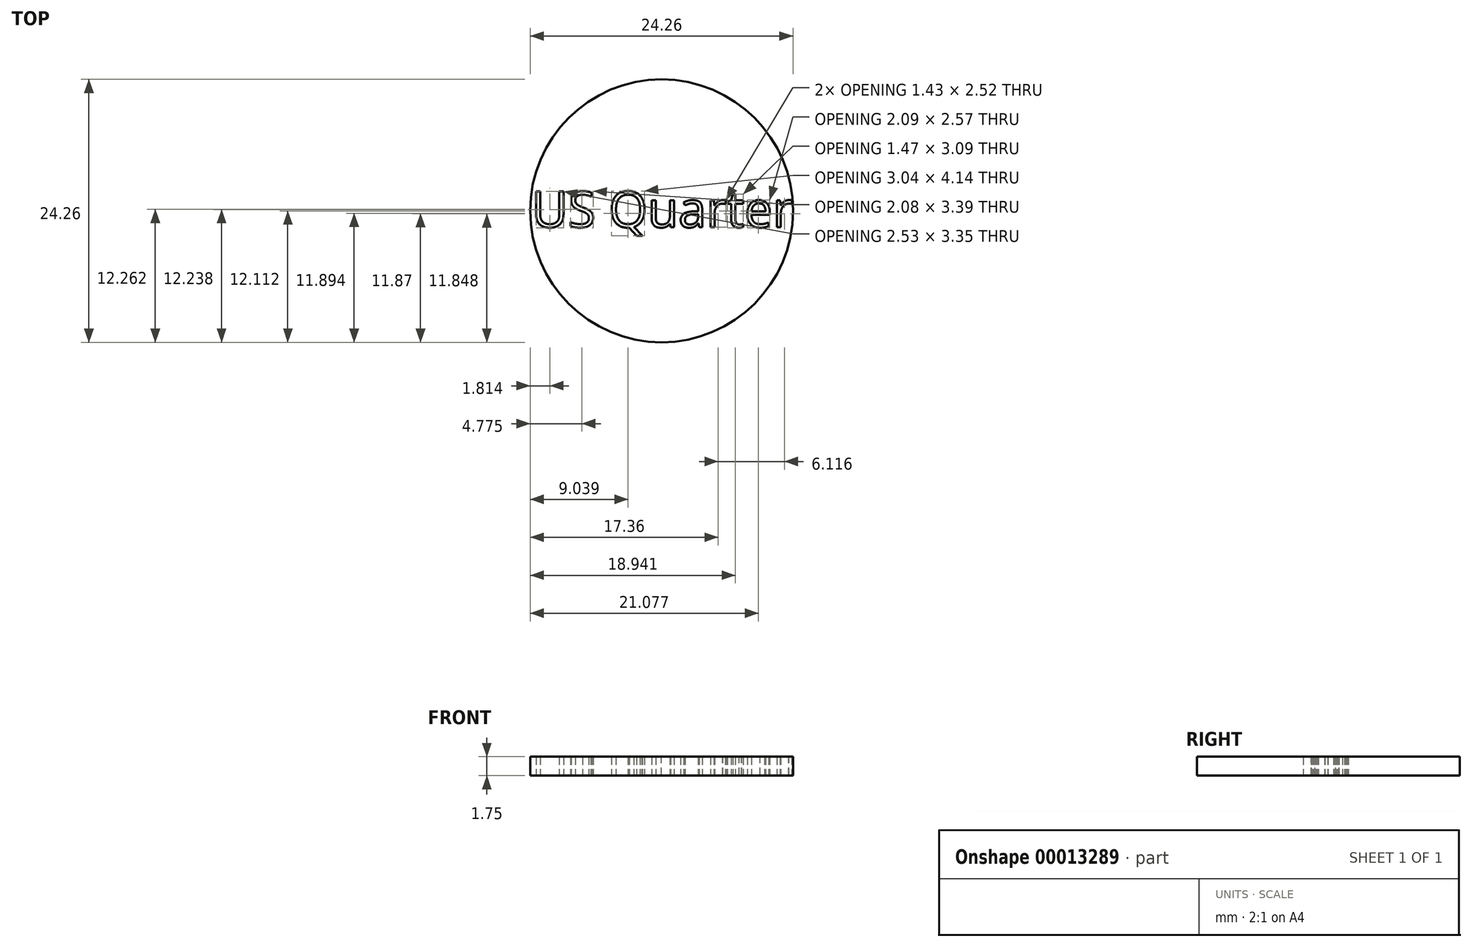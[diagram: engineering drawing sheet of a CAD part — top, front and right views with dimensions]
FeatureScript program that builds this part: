
annotation { "Feature Type Name" : "Feature", "Feature Type Description" : "" }
export const myFeature = defineFeature(function(context is Context, id is Id, definition is map)
    precondition{}
    {
        {
            var Q0;
            Q0=qCreatedBy(makeId("Top.planeOp"),FACE);
            var sketch = newSketch(context, id + "F0", { "sketchPlane" : qUnion([Q0])});
            skCircle(sketch, "E0", {"center": v(0, 0) * mm, "radius": 12.13 * mm});
            skText(sketch, "E1", { "text": "US Quarter", "fontName": "OpenSans-Regular.ttf"});
            const initialGuessF0  = {"E1": [-0.012, -0.00152, 1, 0, 0.00333]};
            skSetInitialGuess(sketch, initialGuessF0);
            skSolve(sketch);
        }
        {
            var Q0;
            Q0=makeQuery(id+"F0.imprint","IMPRINT",FACE,{"disambiguationData":[TD([[makeQuery(id+"F0.imprint","IMPRINT",EDGE,{"derivedFrom":sQuery(id+"F0.wireOp",EDGE,"E0")}),1.0]])]});
            var Q1;
            Q1=makeQuery(id+"F0.imprint","IMPRINT",FACE,{"disambiguationData":[TD([[makeQuery(id+"F0.imprint","IMPRINT",EDGE,{"derivedFrom":sQuery(id+"F0.wireOp",EDGE,"E1.sketch_text.stroke-51")}),1.0]])]});
            var Q2;
            Q2=makeQuery(id+"F0.imprint","IMPRINT",FACE,{"disambiguationData":[TD([[makeQuery(id+"F0.imprint","IMPRINT",EDGE,{"derivedFrom":sQuery(id+"F0.wireOp",EDGE,"E1.sketch_text.stroke-95")}),1.0]])]});
            var Q3;
            Q3=makeQuery(id+"F0.imprint","IMPRINT",FACE,{"disambiguationData":[TD([[makeQuery(id+"F0.imprint","IMPRINT",EDGE,{"derivedFrom":sQuery(id+"F0.wireOp",EDGE,"E1.sketch_text.stroke-149")}),1.0]])]});
            extrude(context, id + "F1", {"entities" : qUnion([Q0, Q1, Q2, Q3]), "depth" : 1.75 * mm});
        }
    });
